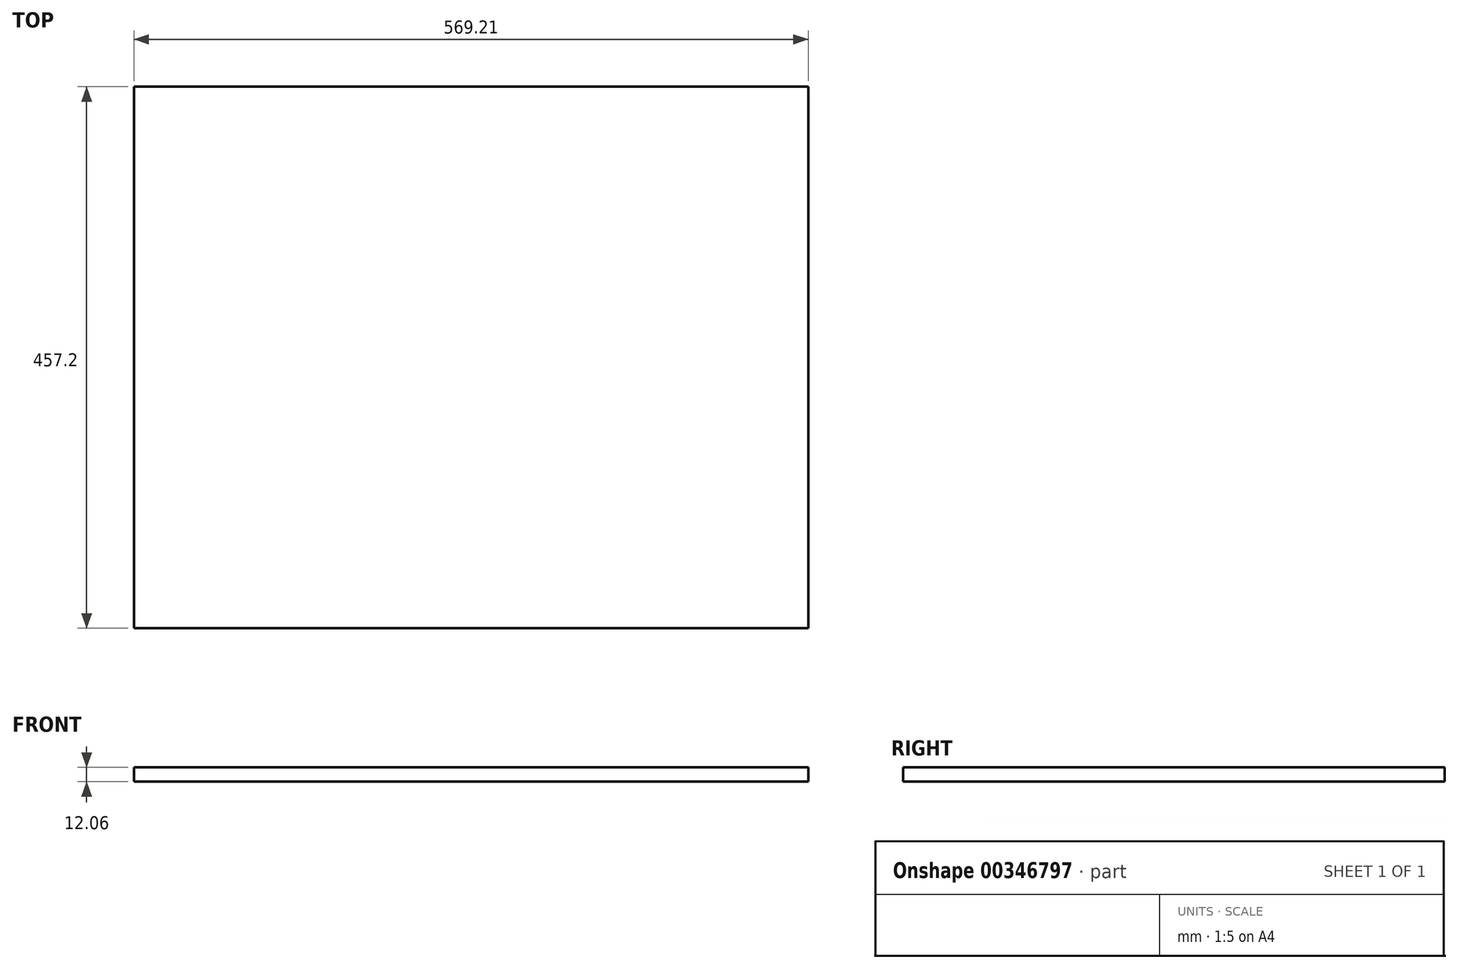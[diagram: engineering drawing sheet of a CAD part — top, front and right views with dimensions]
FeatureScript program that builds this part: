
annotation { "Feature Type Name" : "Feature", "Feature Type Description" : "" }
export const myFeature = defineFeature(function(context is Context, id is Id, definition is map)
    precondition{}
    {
        {
            var Q0;
            Q0=qCreatedBy(makeId("Top.planeOp"),FACE);
            var sketch = newSketch(context, id + "F0", { "sketchPlane" : qUnion([Q0])});
            skLineSegment(sketch, "E0.bottom", {"start": v(0, 0) * mm, "end": v(569.21, 0) * mm});
            skLineSegment(sketch, "E0.top", {"start": v(0, 457.2) * mm, "end": v(569.21, 457.2) * mm});
            skLineSegment(sketch, "E0.left", {"start": v(0, 0) * mm, "end": v(0, 457.2) * mm});
            skLineSegment(sketch, "E0.right", {"start": v(569.21, 0) * mm, "end": v(569.21, 457.2) * mm});
            skLineSegment(sketch, "E1", {"start": v(284.6, 457.2) * mm, "end": v(284.6, 0) * mm, "construction": true});
            skSolve(sketch);
        }
        {
            var Q0;
            Q0 = qSketchRegion(id + "F0", true);
            extrude(context, id + "F1", {"entities" : qUnion([Q0]), "depth" : 12.06 * mm});
        }
    });
